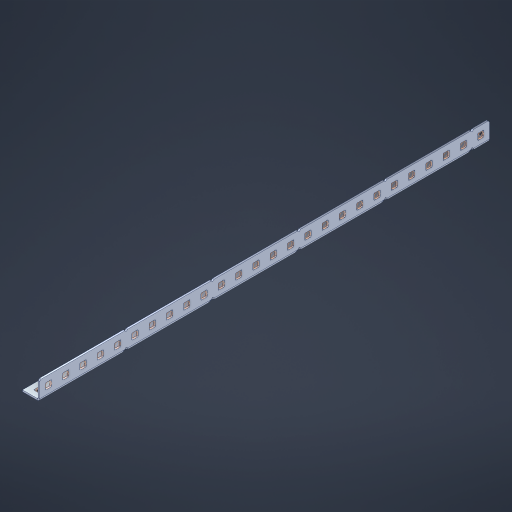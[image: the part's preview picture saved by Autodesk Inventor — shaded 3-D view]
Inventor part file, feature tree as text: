
AUTODESK INVENTOR PART (.ipt)
format: ipt  version: 2023 (Build 270158000, 158)  size: 871,936 bytes
history: native  units: in
note: dims shown in document units (in); Inventor stores cm internally (conversion verified against a paired STEP export)
features: other x57, extrude x51, sheet_metal_op x10, sketch x8, mirror x1, pattern_linear x1, chamfer x1
ambient origin geometry x8: Origin, YZ Plane, XZ Plane, XY Plane, X Axis, Y Axis, Z Axis, Center Point
bodies: Solid1 (feature_tree), Body (feature_tree)
feature tree (129):
  other  "Flange Pattern Plane"
  sheet_metal_op  "Flange Pattern"
  sheet_metal_op  "Body Pattern"
  other  "Arc Length"
  mirror  "Notch Mirror"
  pattern_linear  "Notch Pattern"  Spacing1=0.1875in  [1 undecoded]
  chamfer  "End Chamfer"
  extrude  "Half Cut"  Depth=0.0469in
  sketch  "Sketch1"  dims[d0=2.5in]
  other  "Plate1"
  sketch  "Sketch2"  dims[d1=13.0in]
  other  "Plate2"
  sheet_metal_op  "Bend1"
  sheet_metal_op  "Corner1"
  sketch  "Sketch3"  dims[d2=0.0469in]
  other  "Flange Pattern Sketch"
  sketch  "Sketch7"  dims[d3=0.0469in]
  other  "Srf1"
  other  "Srf2"
  sketch  "Sketch8"  dims[d4=0.0234in]
  sketch  "Sketch9"  dims[d5=0.0938in]
  other  "Srf91"
  sheet_metal_op  "Body Pattern Sketch"
  other  "Srf92"
  sketch  "Sketch13"  dims[d6=0.0469in]
  sketch  "Sketch14"  dims[d7=0.5in d8=90.0deg d9=0.0312in d10=0.1875in d11=0.0469in d12=0.0469in d16=0.182in d17=0.02in d18=0.0469in d19=0.0in d20=0.25in d21=0.25in d46=0.172in d47=1.0in d48=0.0in d49=0.182in d50=0.02in d51=0.25in d52=0.25in d53=0.0469in d54=0.0in d55=0.172in d56=1.0in d57=0.0in d60=10.2362in d62=0.5in d63=0.3937in d65=0.5in d85=0.1227in d86=0.1659in d88=0.04in d89=0.0469in d90=0.0in d91=0.04in d92=0.0491in d95=2.5in d96=0.04in d97=0.25in d98=45.0deg d101=0.0in d102=2.497in d131=0.5in d132=10.2362in d134=0.5in d139=0.5in]
  other  "Srf856"
  other  "Srf1310"
  other  "Srf1311"
  other  "Srf1312"
  other  "Srf1376"
  other  "Srf1377"
  other  "Srf1728"
  other  "Srf1755"
  other  "Srf1878"
  other  "Srf1879"
  other  "Srf1880"
  other  "Srf1881"
  other  "Srf1882"
  other  "Srf1883"
  other  "Srf1884"
  other  "Srf1885"
  other  "Srf1886"
  other  "Srf1887"
  other  "Srf1888"
  other  "Srf1889"
  other  "Srf1890"
  other  "Srf1891"
  other  "Srf1892"
  other  "Srf1893"
  other  "Srf1894"
  other  "Srf1895"
  other  "Srf1896"
  other  "Srf1897"
  other  "Srf1942"
  other  "Srf1943"
  other  "Srf1944"
  other  "Srf1945"
  other  "Srf1946"
  other  "Srf1947"
  other  "Srf1948"
  other  "Srf1949"
  other  "Srf1950"
  other  "Srf1951"
  other  "Srf1952"
  other  "Srf1953"
  other  "Srf1954"
  other  "Srf1955"
  other  "Srf1956"
  other  "Srf1957"
  other  "Srf1958"
  other  "Srf1959"
  other  "Srf1960"
  other  "Srf1961"
  sheet_metal_op  "Flange Stamp"
  sheet_metal_op  "Flange Circle"
  sheet_metal_op  "Body Stamp"
  sheet_metal_op  "Body Circle"
  sheet_metal_op  "Notch"
  extrude  "ExtrusionSrf2"  Depth=0.0469in
  extrude  "ExtrusionSrf92"  Depth=0.5in
  extrude  "ExtrusionSrf856"  Depth=0.02in
  extrude  "ExtrusionSrf1310"  Depth=0.0469in
  extrude  "ExtrusionSrf1311"  TaperAngle=0.0deg  [1 undecoded]
  extrude  "ExtrusionSrf1312"  Depth=0.5in
  extrude  "ExtrusionSrf1376"  Depth=0.5in
  extrude  "ExtrusionSrf1377"  Depth=0.5in
  extrude  "ExtrusionSrf1728"  Depth=0.5in TaperAngle=0.0deg
  extrude  "ExtrusionSrf1755"  Depth=0.5in
  extrude  "ExtrusionSrf1878"  Depth=0.02in
  extrude  "ExtrusionSrf1879"  Depth=0.5in
  extrude  "ExtrusionSrf1880"  Depth=0.5in
  extrude  "ExtrusionSrf1881"  Depth=0.0469in
  extrude  "ExtrusionSrf1882"  TaperAngle=0.0deg  [1 undecoded]
  extrude  "ExtrusionSrf1883"  Depth=0.5in
  extrude  "ExtrusionSrf1884"  Depth=0.5in TaperAngle=0.0deg
  extrude  "ExtrusionSrf1885"  Depth=0.5in
  extrude  "ExtrusionSrf1886"  Depth=0.5in
  extrude  "ExtrusionSrf1887"  Depth=0.5in
  extrude  "ExtrusionSrf1888"  Depth=0.5in
  extrude  "ExtrusionSrf1889"  Depth=0.5in
  extrude  "ExtrusionSrf1890"  Depth=0.0469in
  extrude  "ExtrusionSrf1891"  TaperAngle=0.0deg  [1 undecoded]
  extrude  "ExtrusionSrf1892"  Depth=0.5in
  extrude  "ExtrusionSrf1893"  Depth=0.5in
  extrude  "ExtrusionSrf1894"  Depth=0.5in
  extrude  "ExtrusionSrf1895"  Depth=0.5in TaperAngle=45.0deg
  extrude  "ExtrusionSrf1896"  TaperAngle=0.0deg  [1 undecoded]
  extrude  "ExtrusionSrf1897"  Depth=0.5in
  extrude  "ExtrusionSrf1942"  Depth=0.5in
  extrude  "ExtrusionSrf1943"  Depth=0.5in
  extrude  "ExtrusionSrf1944"  Depth=0.5in
  extrude  "ExtrusionSrf1945"  Depth=0.5in
  extrude  "ExtrusionSrf1946"  [1 undecoded]
  extrude  "ExtrusionSrf1947"  [1 undecoded]
  extrude  "ExtrusionSrf1948"  [1 undecoded]
  extrude  "ExtrusionSrf1949"  [1 undecoded]
  extrude  "ExtrusionSrf1950"  [1 undecoded]
  extrude  "ExtrusionSrf1951"  [1 undecoded]
  extrude  "ExtrusionSrf1952"  [1 undecoded]
  extrude  "ExtrusionSrf1953"  [1 undecoded]
  extrude  "ExtrusionSrf1954"  [1 undecoded]
  extrude  "ExtrusionSrf1955"  [1 undecoded]
  extrude  "ExtrusionSrf1956"  [1 undecoded]
  extrude  "ExtrusionSrf1957"  [1 undecoded]
  extrude  "ExtrusionSrf1958"  [1 undecoded]
  extrude  "ExtrusionSrf1959"  [1 undecoded]
  extrude  "ExtrusionSrf1960"  [1 undecoded]
  extrude  "ExtrusionSrf1961"  [1 undecoded]
note: 21 required parameter values undecoded (feature->parameter linkage not recoverable at this tier; creation-order binding heuristic only, values carry confidence <= 0.55)
